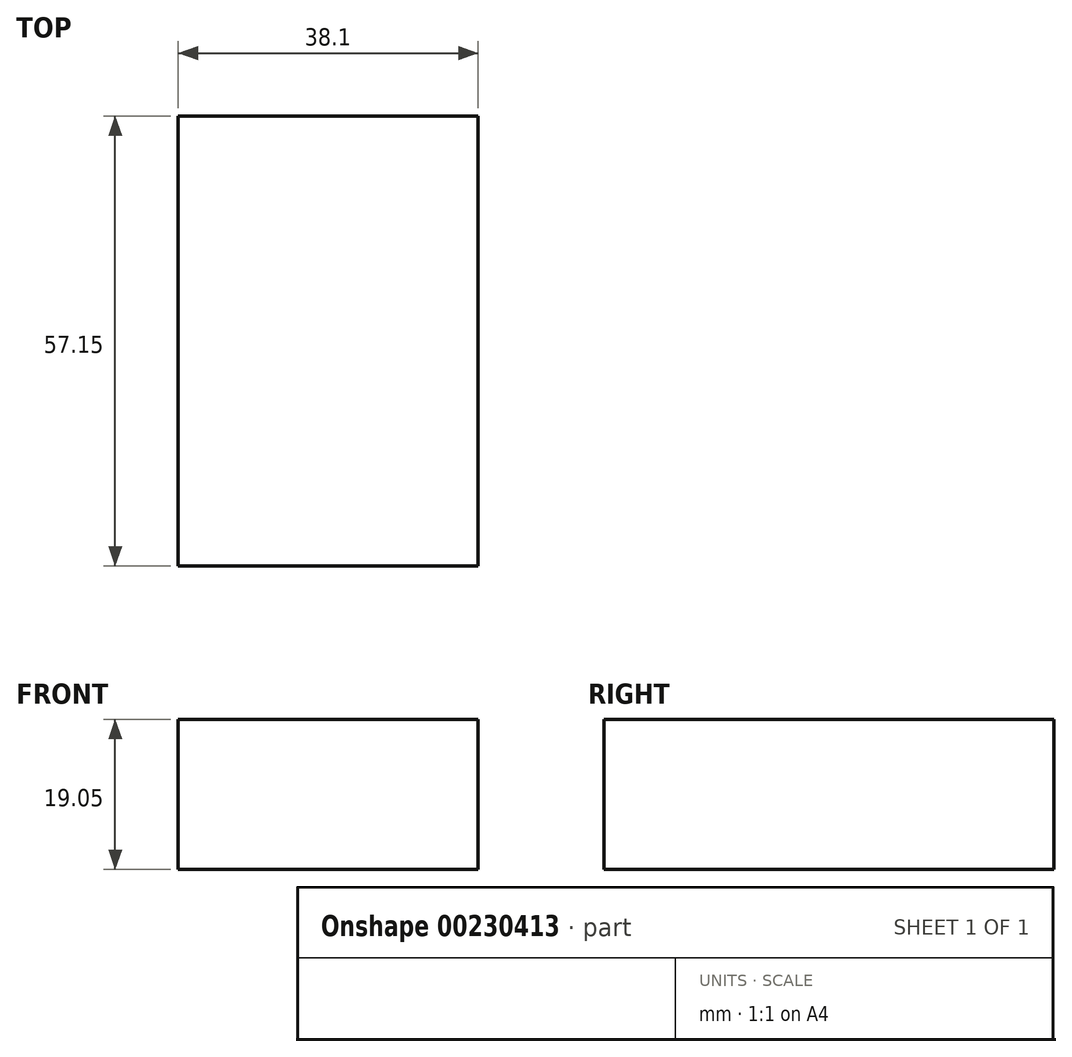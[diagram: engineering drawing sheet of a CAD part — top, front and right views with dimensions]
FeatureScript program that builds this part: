
annotation { "Feature Type Name" : "Feature", "Feature Type Description" : "" }
export const myFeature = defineFeature(function(context is Context, id is Id, definition is map)
    precondition{}
    {
        {
            var Q0;
            Q0=qCreatedBy(makeId("Top.planeOp"),FACE);
            var sketch = newSketch(context, id + "F0", { "sketchPlane" : qUnion([Q0])});
            skLineSegment(sketch, "E0.bottom", {"start": v(-38.1, 0) * mm, "end": v(0, 0) * mm});
            skLineSegment(sketch, "E0.top", {"start": v(-38.1, 57.15) * mm, "end": v(0, 57.15) * mm});
            skLineSegment(sketch, "E0.left", {"start": v(-38.1, 0) * mm, "end": v(-38.1, 57.15) * mm});
            skLineSegment(sketch, "E0.right", {"start": v(0, 0) * mm, "end": v(0, 57.15) * mm});
            skSolve(sketch);
        }
        {
            var Q0;
            Q0=makeQuery(id+"F0.imprint","IMPRINT",FACE,{"disambiguationData":[TD([[makeQuery(id+"F0.imprint","IMPRINT",EDGE,{"derivedFrom":sQuery(id+"F0.wireOp",EDGE,"E0.bottom")}),1.0]])]});
            extrude(context, id + "F1", {"entities" : qUnion([Q0]), "depth" : 19.05 * mm});
        }
    });
